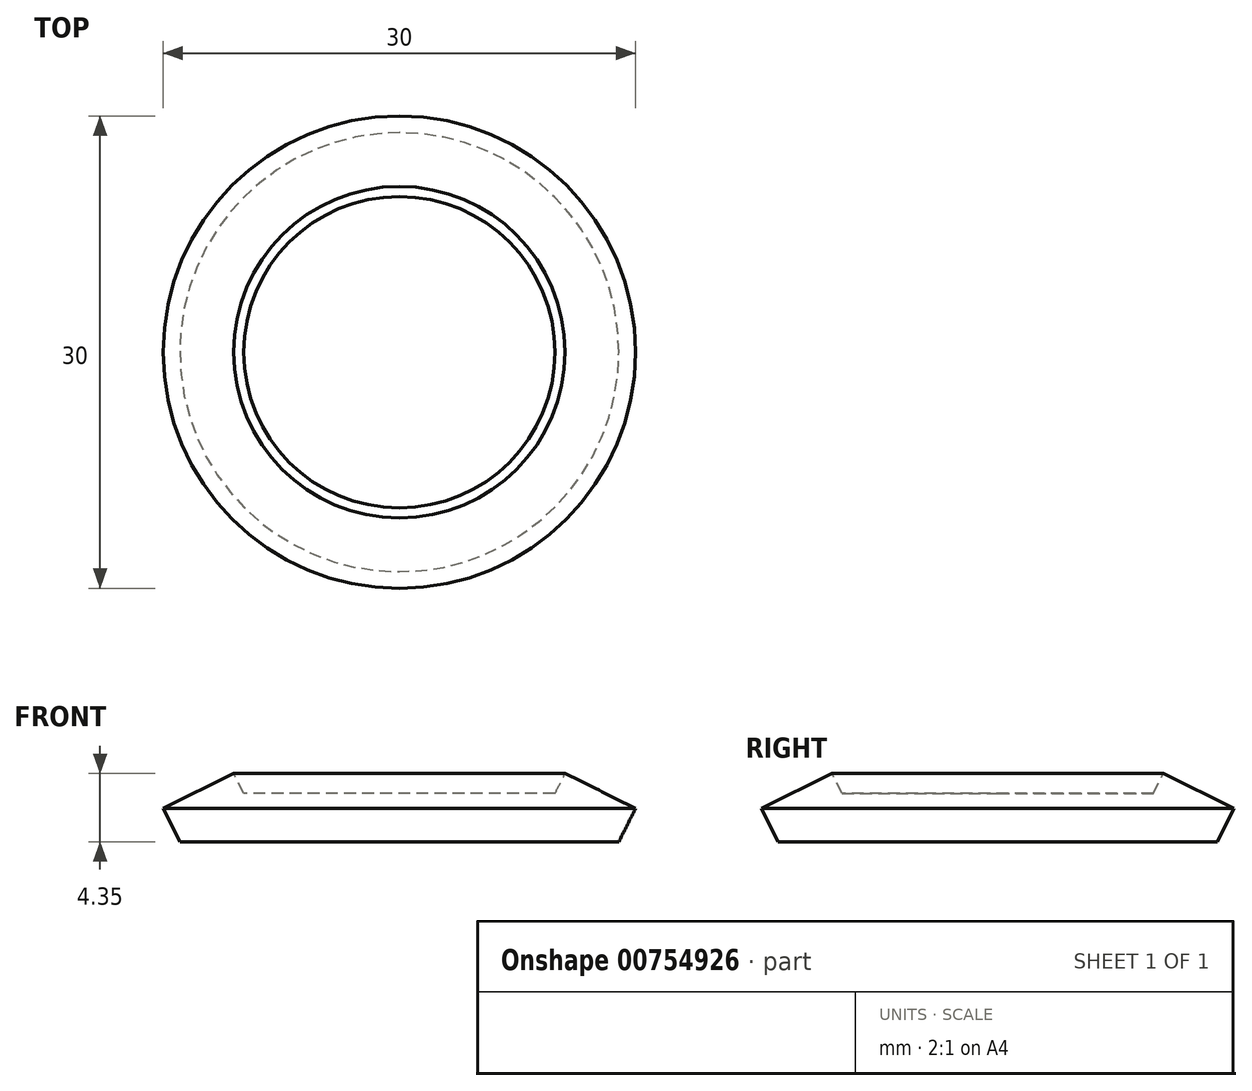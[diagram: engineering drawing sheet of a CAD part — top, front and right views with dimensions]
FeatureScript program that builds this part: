
annotation { "Feature Type Name" : "Feature", "Feature Type Description" : "" }
export const myFeature = defineFeature(function(context is Context, id is Id, definition is map)
    precondition{}
    {
        {
            var Q0;
            Q0=qCreatedBy(makeId("Front.planeOp"),FACE);
            var sketch = newSketch(context, id + "F0", { "sketchPlane" : qUnion([Q0])});
            skLineSegment(sketch, "E0", {"start": v(0, 9.59) * mm, "end": v(0, -2.57) * mm, "construction": true});
            skLineSegment(sketch, "E1", {"start": v(0, 8.62) * mm, "end": v(15, 1.12) * mm, "construction": true});
            skLineSegment(sketch, "E2", {"start": v(0, -1) * mm, "end": v(13.94, -1) * mm});
            skLineSegment(sketch, "E3", {"start": v(13.94, -1) * mm, "end": v(15.45, 2.01) * mm});
            skLineSegment(sketch, "E4", {"start": v(15.45, 2.01) * mm, "end": v(10.84, 3.98) * mm});
            skLineSegment(sketch, "E5", {"start": v(10.84, 3.98) * mm, "end": v(9.89, 2.07) * mm});
            skLineSegment(sketch, "E6", {"start": v(9.89, 2.07) * mm, "end": v(0, 2.07) * mm});
            skPoint(sketch, "E7", {"position": v(14.44, 0) * mm});
            skPoint(sketch, "E8", {"position": v(15, 1.12) * mm});
            skPoint(sketch, "E9", {"position": v(10.14, 2.57) * mm});
            skLineSegment(sketch, "E10", {"start": v(0, 8.62) * mm, "end": v(15.45, 2.01) * mm, "construction": true});
            skLineSegment(sketch, "E11", {"start": v(0, 8.62) * mm, "end": v(14.44, 0) * mm, "construction": true});
            skPoint(sketch, "E12", {"position": v(10.53, 3.35) * mm});
            skLineSegment(sketch, "E13", {"start": v(0, 2.07) * mm, "end": v(0, -1) * mm});
            skSolve(sketch);
        }
        {
            var Q0;
            Q0=qCreatedBy(makeId("Front.planeOp"),FACE);
            var sketch = newSketch(context, id + "F1", { "sketchPlane" : qUnion([Q0])});
            skLineSegment(sketch, "E14.0", {"start": v(9.89, 2.07) * mm, "end": v(0, 2.07) * mm});
            skLineSegment(sketch, "E15.0", {"start": v(10.53, 3.35) * mm, "end": v(9.89, 2.07) * mm});
            skLineSegment(sketch, "E16.0", {"start": v(10.53, 3.35) * mm, "end": v(15, 1.12) * mm});
            skLineSegment(sketch, "E17.0", {"start": v(13.94, -1) * mm, "end": v(15, 1.12) * mm});
            skLineSegment(sketch, "E18.0", {"start": v(0, -1) * mm, "end": v(13.94, -1) * mm});
            skPoint(sketch, "E19.orphan", {"position": v(0, 8.62) * mm});
            skPoint(sketch, "E20.orphan", {"position": v(15.45, 2.01) * mm});
            skLineSegment(sketch, "E21.0", {"start": v(0, 2.07) * mm, "end": v(0, -1) * mm});
            skSolve(sketch);
        }
        {
            var Q0;
            Q0=qSketchRegion(id+"F1",true);
            var Q1;
            Q1=sQuery(id+"F0.wireOp",EDGE,"E0");
            revolve(context, id + "F2", {"entities" : qUnion([Q0]), "axis" : qUnion([Q1]), "revolveType" : RevolveType.FULL});
        }
    });
